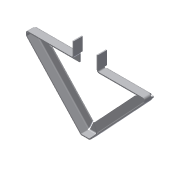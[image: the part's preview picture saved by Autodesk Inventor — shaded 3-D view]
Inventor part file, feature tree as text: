
AUTODESK INVENTOR PART (.ipt)
format: ipt  version: 2015 (Build 190159000, 159)  size: 335,872 bytes
history: native  units: in
note: dims shown in document units (in); Inventor stores cm internally (conversion verified against a paired STEP export)
features: sheet_metal_op x6, sketch x3, other x3, hole x1
ambient origin geometry x8: Origin, YZ Plane, XZ Plane, XY Plane, X Axis, Y Axis, Z Axis, Center Point
bodies: Solid1 (feature_tree)
feature tree (13):
  sheet_metal_op  "Contour Flange1"
  sheet_metal_op  "Flange1"
  hole  "Hole2"  [1 undecoded]
  sketch  "Sketch1"  dims[d0=0.5in d1=1.0in]
  other  "Plate1"
  sheet_metal_op  "Bend1"
  sheet_metal_op  "Corner1"
  sketch  "Sketch2"  dims[d2=7.0in]
  other  "Plate2"
  sheet_metal_op  "Bend2"
  sheet_metal_op  "Corner2"
  sketch  "Sketch4"  dims[d4=0.12in d5=0.06in d6=0.24in d7=0.12in d8=1.0in d9=0.12in d10=0.12in d11=0.48in d12=0.12in d13=0.12in d14=0.12in d15=0.06in d16=0.24in d17=0.12in d18=1.0in d19=90.0deg d20=0.12in d21=0.48in d22=0.12in d23=0.12in d24=2.792in d33=1.75in d34=0.1in d35=0.75in d36=0.375in d37=0.25in d38=0.5635in d39=0.1in d40=0.0in]
  other  "Definition1"
note: 1 required parameter value undecoded (feature->parameter linkage not recoverable at this tier; creation-order binding heuristic only, values carry confidence <= 0.55)
